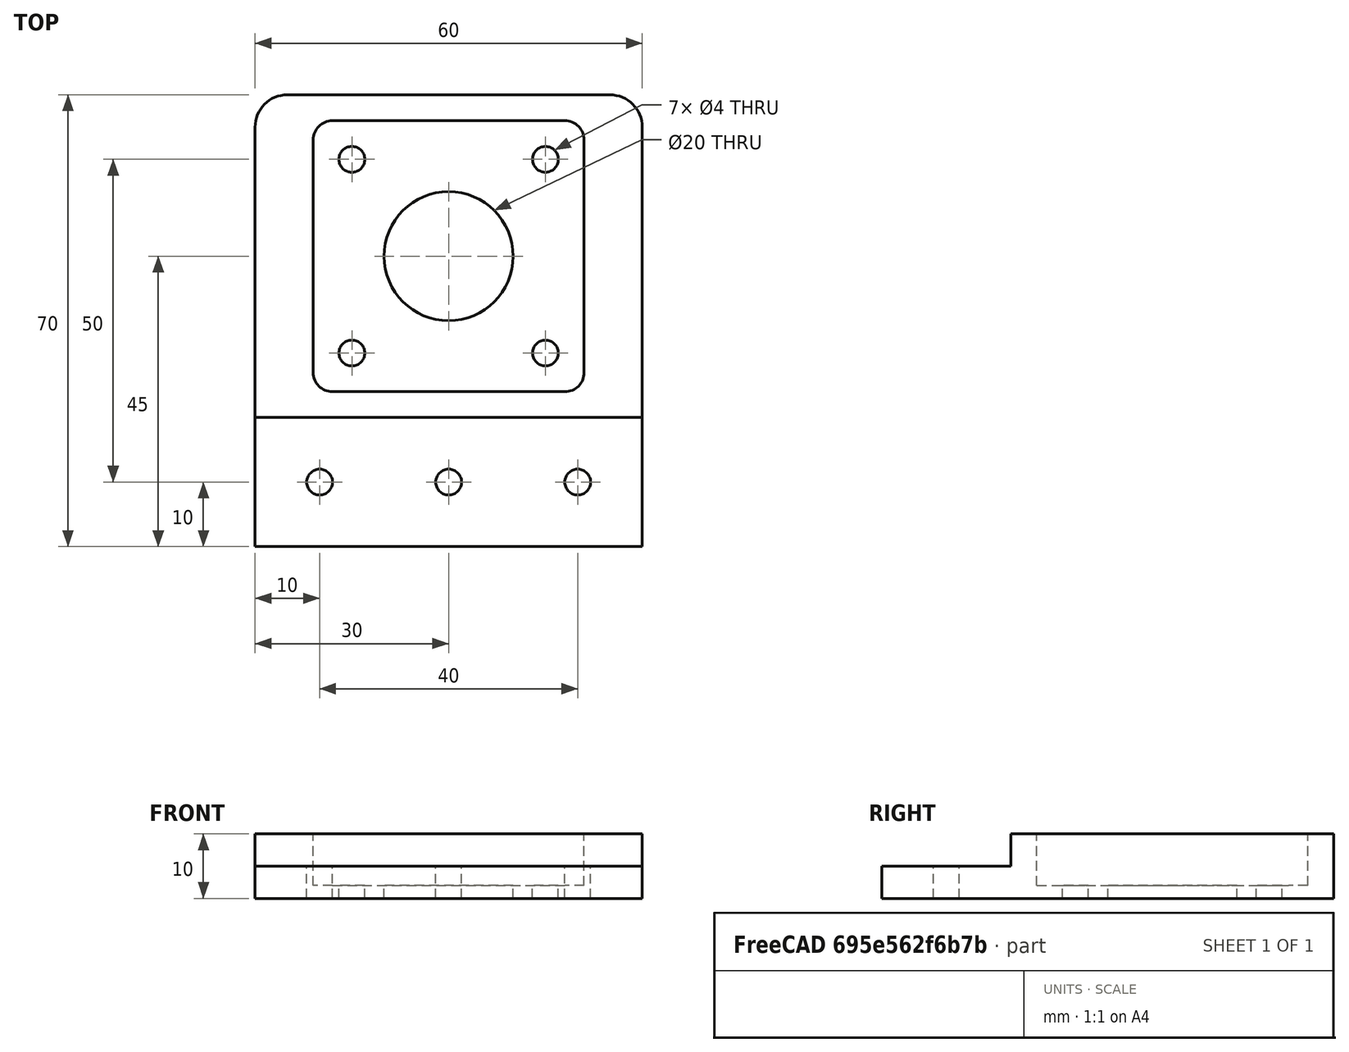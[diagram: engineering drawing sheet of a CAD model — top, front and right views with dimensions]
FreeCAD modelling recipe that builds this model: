
FCSTD DOCUMENT  (FreeCAD 0.19R24276 (Git))
Label: motorBowder
License: All rights reserved
LicenseURL: http://en.wikipedia.org/wiki/All_rights_reserved
objects: Part::Cut×10, Part::Cylinder×8, Part::Box×3, Part::Fillet×3
note: 24 computed .brp shape members not serialized (recipe doc carries the construction recipe); baked Part::Feature solids carry a one-line shape summary decoded from their .brp

FEATURE [Part::Box] Box  label="Cube"
  AttacherType = Attacher::AttachEngine3D
  Height = 10
  Length = 60
  Width = 70
FEATURE [Part::Box] Box001  label="Cube001"
  AttacherType = Attacher::AttachEngine3D
  Height = 10
  Length = 60
  Placement = pos=(0,0,5) rot=(0,0,1;0rad)
  Width = 20
FEATURE [Part::Cut] Cut
  Base = -> Box
  Tool = -> Box001
FEATURE [Part::Cylinder] Cylinder
  Angle = 360
  AttacherType = Attacher::AttachEngine3D
  Height = 10
  Placement = pos=(10,10,-1) rot=(0,0,1;0rad)
  Radius = 2
FEATURE [Part::Cylinder] Cylinder001
  Angle = 360
  AttacherType = Attacher::AttachEngine3D
  Height = 10
  Placement = pos=(30,10,-1) rot=(0,0,1;0rad)
  Radius = 2
FEATURE [Part::Cylinder] Cylinder002
  Angle = 360
  AttacherType = Attacher::AttachEngine3D
  Height = 10
  Placement = pos=(50,10,-1) rot=(0,0,1;0rad)
  Radius = 2
FEATURE [Part::Cut] Cut001
  Base = -> Cut
  Tool = -> Cylinder
FEATURE [Part::Cut] Cut002
  Base = -> Cut001
  Tool = -> Cylinder001
FEATURE [Part::Cut] Cut003
  Base = -> Cut002
  Tool = -> Cylinder002
FEATURE [Part::Box] Box002  label="Cube002"
  AttacherType = Attacher::AttachEngine3D
  Height = 10
  Length = 42
  Placement = pos=(9,24,2) rot=(0,0,1;0rad)
  Width = 42
FEATURE [Part::Cut] Cut004
  Base = -> Cut003
  Tool = -> Box002
FEATURE [Part::Cylinder] Cylinder003
  Angle = 360
  AttacherType = Attacher::AttachEngine3D
  Height = 10
  Placement = pos=(15,30,-1) rot=(0,0,1;0rad)
  Radius = 2
FEATURE [Part::Cylinder] Cylinder004
  Angle = 360
  AttacherType = Attacher::AttachEngine3D
  Height = 10
  Placement = pos=(15,60,-1) rot=(0,0,1;0rad)
  Radius = 2
FEATURE [Part::Cylinder] Cylinder005
  Angle = 360
  AttacherType = Attacher::AttachEngine3D
  Height = 10
  Placement = pos=(45,60,-1) rot=(0,0,1;0rad)
  Radius = 2
FEATURE [Part::Cylinder] Cylinder006
  Angle = 360
  AttacherType = Attacher::AttachEngine3D
  Height = 10
  Placement = pos=(45,30,-1) rot=(0,0,1;0rad)
  Radius = 2
FEATURE [Part::Cut] Cut005
  Base = -> Cut004
  Tool = -> Cylinder003
FEATURE [Part::Cut] Cut006
  Base = -> Cut005
  Tool = -> Cylinder004
FEATURE [Part::Cut] Cut007
  Base = -> Cut006
  Tool = -> Cylinder005
FEATURE [Part::Cut] Cut008
  Base = -> Cut007
  Tool = -> Cylinder006
FEATURE [Part::Fillet] Fillet
  Base = -> Cut008
  Edges = 1 edges r=5: [Edge5]
FEATURE [Part::Fillet] Fillet001
  Base = -> Fillet
  Edges = 1 edges r=5: [Edge35]
FEATURE [Part::Fillet] Fillet002
  Base = -> Fillet001
  Edges = 4 edges r=3: [Edge27,Edge28,Edge30,Edge32]
FEATURE [Part::Cylinder] Cylinder007
  Angle = 360
  AttacherType = Attacher::AttachEngine3D
  Height = 10
  Placement = pos=(30,45,-1) rot=(0,0,1;0rad)
  Radius = 10
FEATURE [Part::Cut] Cut009  label="SujeccionMotor"
  Base = -> Fillet002
  Tool = -> Cylinder007
